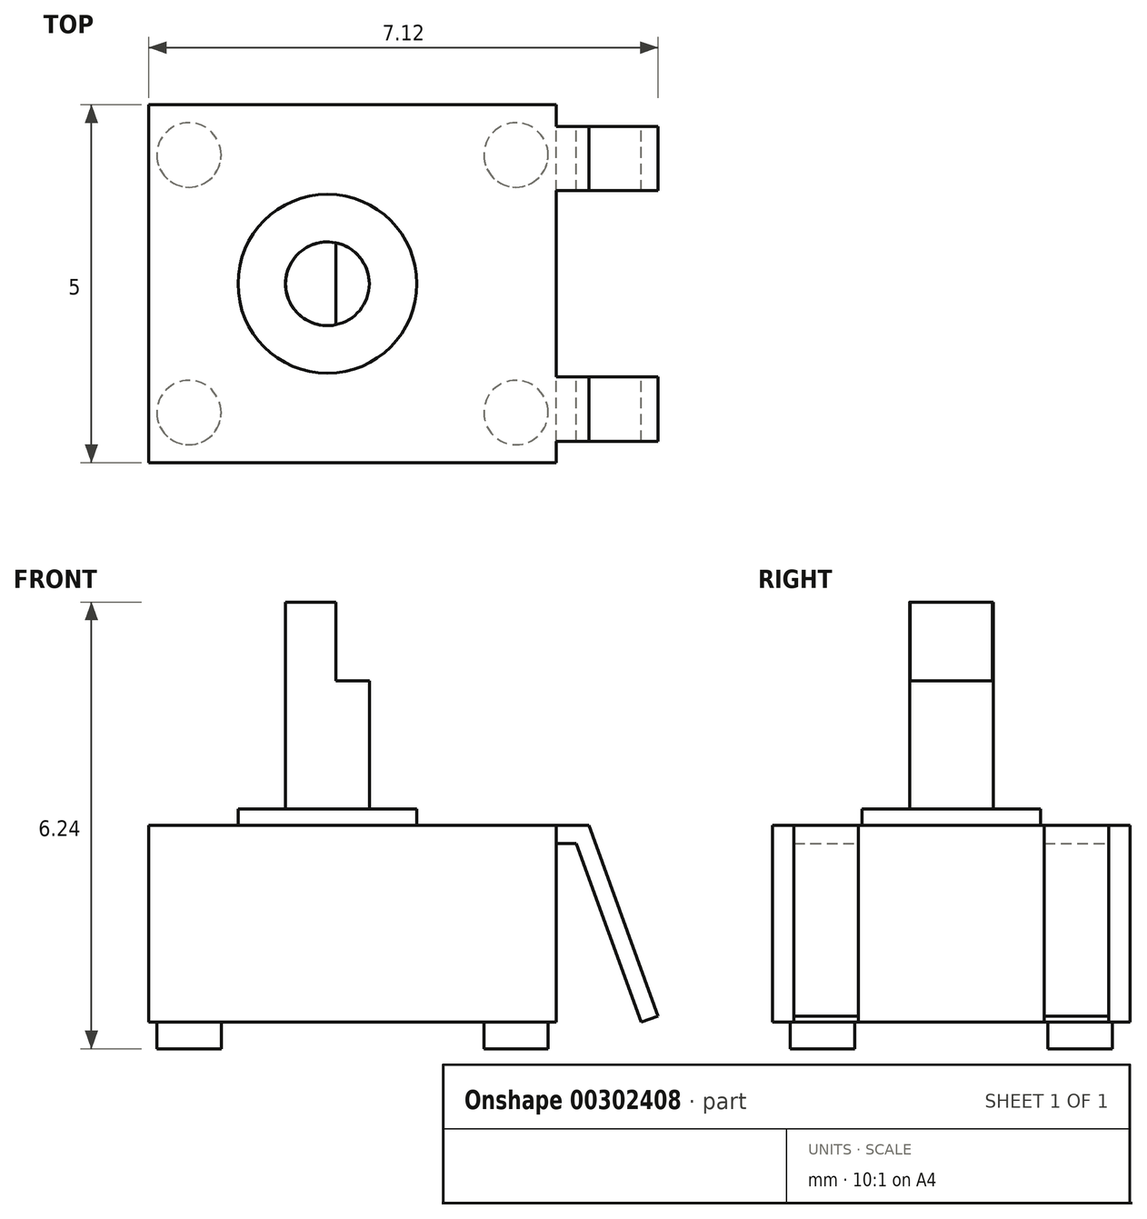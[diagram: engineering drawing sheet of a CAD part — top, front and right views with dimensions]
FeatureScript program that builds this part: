
annotation { "Feature Type Name" : "Feature", "Feature Type Description" : "" }
export const myFeature = defineFeature(function(context is Context, id is Id, definition is map)
    precondition{}
    {
        {
            var Q0;
            Q0=qCreatedBy(makeId("Top.planeOp"),FACE);
            var sketch = newSketch(context, id + "F0", { "sketchPlane" : qUnion([Q0])});
            skLineSegment(sketch, "E0.bottom", {"start": v(-2.5, 2.5) * mm, "end": v(3.2, 2.5) * mm});
            skLineSegment(sketch, "E0.top", {"start": v(-2.5, -2.5) * mm, "end": v(3.2, -2.5) * mm});
            skLineSegment(sketch, "E0.left", {"start": v(-2.5, 2.5) * mm, "end": v(-2.5, -2.5) * mm});
            skLineSegment(sketch, "E0.right", {"start": v(3.2, 2.5) * mm, "end": v(3.2, -2.5) * mm});
            skSolve(sketch);
        }
        {
            var Q0;
            Q0 = qSketchRegion(id + "F0", true);
            extrude(context, id + "F1", {"entities" : qUnion([Q0]), "oppositeDirection" : true, "depth" : 2.75 * mm});
        }
        {
            var Q0;
            Q0=makeQuery(id+"F1.opExtrude","CAP_FACE",FACE,{"disambiguationData":[OSD([sQuery(id+"F0.wireOp",EDGE,"E0.bottom"),sQuery(id+"F0.wireOp",EDGE,"E0.top"),sQuery(id+"F0.wireOp",EDGE,"E0.left"),sQuery(id+"F0.wireOp",EDGE,"E0.right")])],"isStart":true});
            var sketch = newSketch(context, id + "F2", { "sketchPlane" : qUnion([Q0])});
            skCircle(sketch, "E1", {"center": v(0, 0) * mm, "radius": 1.25 * mm});
            skCircle(sketch, "E2", {"center": v(0, 0) * mm, "radius": 0.58 * mm});
            skSolve(sketch);
        }
        {
            var Q0;
            Q0=makeQuery(id+"F2.imprint","IMPRINT",FACE,{"disambiguationData":[TD([[makeQuery(id+"F2.imprint","IMPRINT",EDGE,{"derivedFrom":sQuery(id+"F2.wireOp",EDGE,"E1")}),1.0]])]});
            extrude(context, id + "F3", {"entities" : qUnion([Q0]), "operationType" : NewBodyOperationType.ADD, "depth" : 0.23 * mm});
        }
        {
            var Q0;
            Q0=makeQuery(id+"F3.boolean.opBoolean","SPLIT",FACE,{"disambiguationData":[TD([makeQuery(id+"F3.opExtrude","SWEPT_FACE",FACE,{"disambiguationData":[OSD([sQuery(id+"F2.wireOp",EDGE,"E2")])]})])],"derivedFrom":makeQuery(id+"F1.opExtrude","CAP_FACE",FACE,{"disambiguationData":[OSD([sQuery(id+"F0.wireOp",EDGE,"E0.bottom"),sQuery(id+"F0.wireOp",EDGE,"E0.top"),sQuery(id+"F0.wireOp",EDGE,"E0.left"),sQuery(id+"F0.wireOp",EDGE,"E0.right")])],"isStart":true})});
            extrude(context, id + "F4", {"entities" : qUnion([Q0]), "operationType" : NewBodyOperationType.ADD, "depth" : 3.12 * mm});
        }
        {
            var Q0;
            Q0=makeQuery(id+"F4.opExtrude","CAP_FACE",FACE,{"disambiguationData":[OSD([sQuery(id+"F0.wireOp",EDGE,"E0.bottom"),sQuery(id+"F0.wireOp",EDGE,"E0.top"),sQuery(id+"F0.wireOp",EDGE,"E0.left"),sQuery(id+"F0.wireOp",EDGE,"E0.right")])],"isStart":false});
            var sketch = newSketch(context, id + "F5", { "sketchPlane" : qUnion([Q0])});
            skLineSegment(sketch, "E3", {"start": v(0.11, 0.57) * mm, "end": v(0.12, -0.57) * mm});
            skArc(sketch, "E4", {"start": v(0.11, 0.57) * mm, "mid": v(0.58, 0) * mm, "end": v(0.11, -0.57) * mm});
            skSolve(sketch);
        }
        {
            var Q0;
            Q0 = qSketchRegion(id + "F5", true);
            extrude(context, id + "F6", {"entities" : qUnion([Q0]), "operationType" : NewBodyOperationType.REMOVE, "oppositeDirection" : true, "depth" : 1.1 * mm});
        }
        {
            var Q0;
            Q0=makeQuery(id+"F1.opExtrude","CAP_FACE",FACE,{"disambiguationData":[OSD([sQuery(id+"F0.wireOp",EDGE,"E0.bottom"),sQuery(id+"F0.wireOp",EDGE,"E0.top"),sQuery(id+"F0.wireOp",EDGE,"E0.left"),sQuery(id+"F0.wireOp",EDGE,"E0.right")])],"isStart":false});
            var sketch = newSketch(context, id + "F7", { "sketchPlane" : qUnion([Q0])});
            skCircle(sketch, "E5", {"center": v(2.63, 1.8) * mm, "radius": 0.45 * mm});
            skCircle(sketch, "E6", {"center": v(-1.94, 1.8) * mm, "radius": 0.45 * mm});
            skCircle(sketch, "E7", {"center": v(-1.94, -1.8) * mm, "radius": 0.45 * mm});
            skCircle(sketch, "E8", {"center": v(2.63, -1.8) * mm, "radius": 0.45 * mm});
            skLineSegment(sketch, "E9.bottom", {"start": v(-1.94, -1.8) * mm, "end": v(2.63, -1.8) * mm, "construction": true});
            skLineSegment(sketch, "E9.top", {"start": v(-1.94, 1.8) * mm, "end": v(2.63, 1.8) * mm, "construction": true});
            skLineSegment(sketch, "E9.left", {"start": v(-1.94, -1.8) * mm, "end": v(-1.94, 1.8) * mm, "construction": true});
            skLineSegment(sketch, "E9.right", {"start": v(2.64, -1.8) * mm, "end": v(2.63, 1.8) * mm, "construction": true});
            skPoint(sketch, "E10", {"position": v(-2.5, 0) * mm});
            skPoint(sketch, "E11", {"position": v(0.35, -2.5) * mm});
            skPoint(sketch, "E12", {"position": v(-1.94, 0) * mm});
            skPoint(sketch, "E13", {"position": v(0.35, -1.8) * mm});
            skLineSegment(sketch, "E14", {"start": v(-2.5, 0) * mm, "end": v(-1.94, 0) * mm, "construction": true});
            skLineSegment(sketch, "E15", {"start": v(0.35, -2.5) * mm, "end": v(0.35, -1.8) * mm, "construction": true});
            skSolve(sketch);
        }
        {
            var Q0;
            Q0 = qSketchRegion(id + "F7", true);
            extrude(context, id + "F8", {"entities" : qUnion([Q0]), "operationType" : NewBodyOperationType.ADD, "depth" : 0.37 * mm});
        }
        {
            var Q0;
            Q0=qCreatedBy(makeId("Front.planeOp"),FACE);
            var sketch = newSketch(context, id + "F9", { "sketchPlane" : qUnion([Q0])});
            skLineSegment(sketch, "E16", {"start": v(3.2, 0) * mm, "end": v(3.66, 0) * mm});
            skLineSegment(sketch, "E17", {"start": v(3.66, 0) * mm, "end": v(4.62, -2.66) * mm});
            skLineSegment(sketch, "E18", {"start": v(4.62, -2.66) * mm, "end": v(4.38, -2.75) * mm});
            skLineSegment(sketch, "E19", {"start": v(3.2, -0.25) * mm, "end": v(3.48, -0.25) * mm});
            skLineSegment(sketch, "E20", {"start": v(3.48, -0.25) * mm, "end": v(4.38, -2.75) * mm});
            skLineSegment(sketch, "E21", {"start": v(3.2, 0) * mm, "end": v(3.2, -0.25) * mm});
            skSolve(sketch);
        }
        {
            var Q0;
            Q0 = qSketchRegion(id + "F9", true);
            extrude(context, id + "F10", {"entities" : qUnion([Q0]), "operationType" : NewBodyOperationType.ADD, "depth" : 2.2 * mm, "hasSecondDirection" : true, "secondDirectionOppositeDirection" : true, "secondDirectionDepth" : 2.2 * mm});
        }
        {
            var Q0;
            Q0=qCreatedBy(makeId("Front.planeOp"),FACE);
            var sketch = newSketch(context, id + "F11", { "sketchPlane" : qUnion([Q0])});
            skLineSegment(sketch, "E22.bottom", {"start": v(3.2, 0) * mm, "end": v(4.62, 0) * mm});
            skLineSegment(sketch, "E22.top", {"start": v(3.2, -2.75) * mm, "end": v(4.62, -2.75) * mm});
            skLineSegment(sketch, "E22.left", {"start": v(3.2, 0) * mm, "end": v(3.2, -2.75) * mm});
            skLineSegment(sketch, "E22.right", {"start": v(4.62, 0) * mm, "end": v(4.62, -2.75) * mm});
            skSolve(sketch);
        }
        {
            var Q0;
            Q0 = qSketchRegion(id + "F11", true);
            extrude(context, id + "F12", {"entities" : qUnion([Q0]), "operationType" : NewBodyOperationType.REMOVE, "oppositeDirection" : true, "depth" : 1.3 * mm, "hasSecondDirection" : true, "secondDirectionOppositeDirection" : false, "secondDirectionDepth" : 1.3 * mm});
        }
    });
